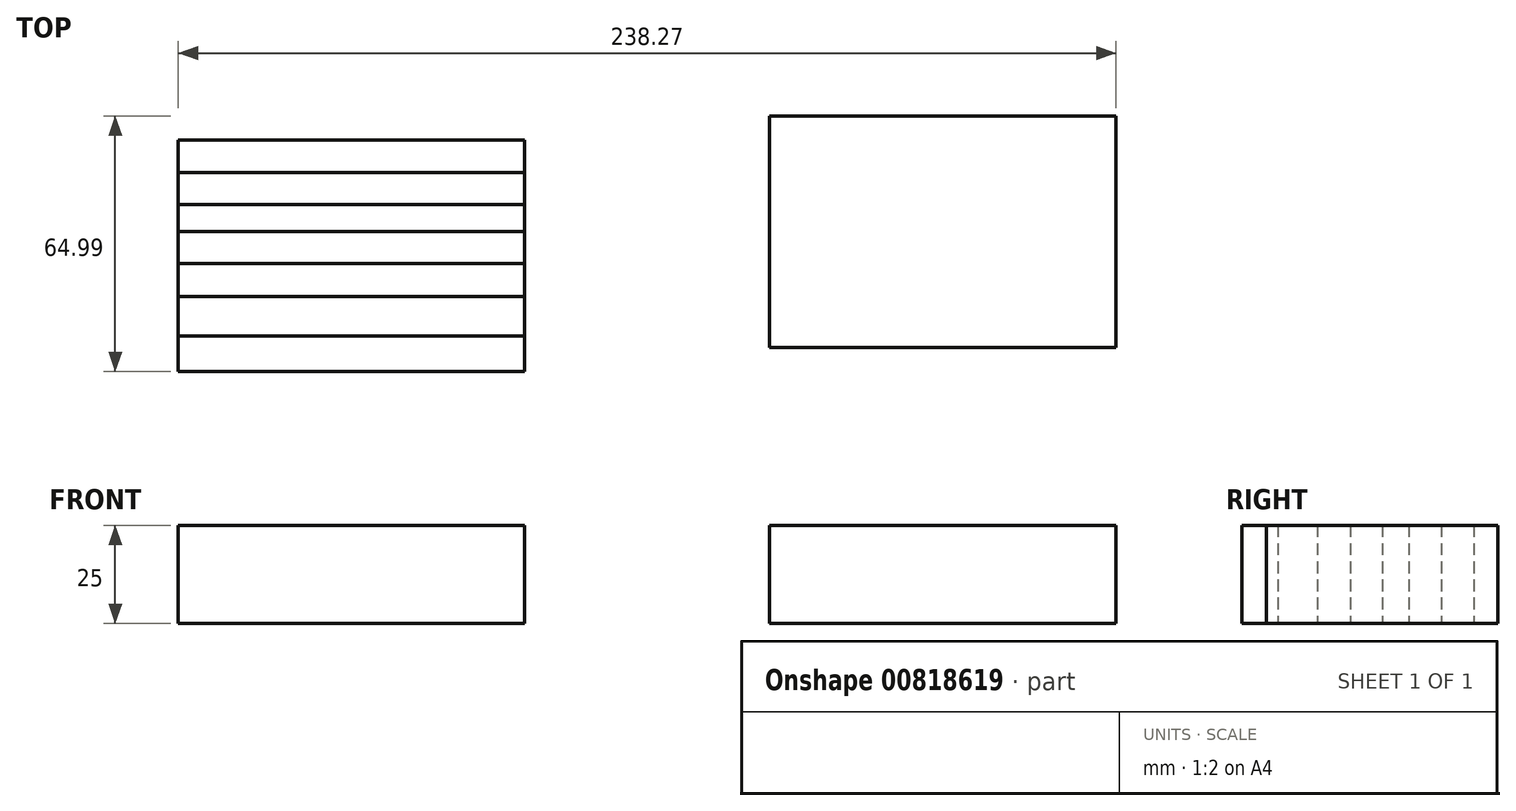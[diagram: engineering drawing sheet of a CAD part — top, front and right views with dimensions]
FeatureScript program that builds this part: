
annotation { "Feature Type Name" : "Feature", "Feature Type Description" : "" }
export const myFeature = defineFeature(function(context is Context, id is Id, definition is map)
    precondition{}
    {
        {
            var Q0;
            Q0=qCreatedBy(makeId("Top.planeOp"),FACE);
            var sketch = newSketch(context, id + "F0", { "sketchPlane" : qUnion([Q0])});
            skLineSegment(sketch, "E0.bottom", {"start": v(-107.96, 31.35) * mm, "end": v(-19.95, 31.35) * mm});
            skLineSegment(sketch, "E0.top", {"start": v(-107.96, -27.48) * mm, "end": v(-19.95, -27.48) * mm});
            skLineSegment(sketch, "E0.left", {"start": v(-107.96, 31.35) * mm, "end": v(-107.96, -27.48) * mm});
            skLineSegment(sketch, "E0.right", {"start": v(-19.95, 31.35) * mm, "end": v(-19.95, -27.48) * mm});
            skLineSegment(sketch, "E1.bottom", {"start": v(42.3, 37.5) * mm, "end": v(130.3, 37.5) * mm});
            skLineSegment(sketch, "E1.top", {"start": v(42.3, -21.32) * mm, "end": v(130.3, -21.32) * mm});
            skLineSegment(sketch, "E1.left", {"start": v(42.3, 37.5) * mm, "end": v(42.3, -21.32) * mm});
            skLineSegment(sketch, "E1.right", {"start": v(130.3, 37.5) * mm, "end": v(130.3, -21.32) * mm});
            skLineSegment(sketch, "E2", {"start": v(-107.96, 23.14) * mm, "end": v(-19.95, 23.14) * mm});
            skLineSegment(sketch, "E3", {"start": v(-107.96, 14.93) * mm, "end": v(-19.95, 14.93) * mm});
            skLineSegment(sketch, "E4", {"start": v(-107.96, 8.1) * mm, "end": v(-19.95, 8.1) * mm});
            skPoint(sketch, "E4.endSnap0", {"position": v(-19.95, 1.94) * mm});
            skLineSegment(sketch, "E5", {"start": v(-107.96, 0) * mm, "end": v(-19.95, 0) * mm});
            skLineSegment(sketch, "E6", {"start": v(-107.96, -8.32) * mm, "end": v(-19.95, -8.32) * mm});
            skLineSegment(sketch, "E7", {"start": v(-107.96, -18.36) * mm, "end": v(-19.95, -18.36) * mm});
            skSolve(sketch);
        }
        {
            var Q0;
            Q0=makeQuery(id+"F0.imprint","IMPRINT",FACE,{"disambiguationData":[TD([[makeQuery(id+"F0.imprint","IMPRINT",EDGE,{"derivedFrom":sQuery(id+"F0.wireOp",EDGE,"E1.bottom")}),-1.0]])]});
            extrude(context, id + "F1", {"entities" : qUnion([Q0]), "depth" : 25 * mm, "offsetDistance" : 25 * mm});
        }
        {
            var Q0;
            {var subQ0=sQuery(id+"F0.wireOp",EDGE,"E0.bottom");Q0=makeQuery(id+"F0.imprint","IMPRINT",FACE,{"disambiguationData":[TD([[makeQuery(id+"F0.imprint","IMPRINT",EDGE,{"derivedFrom":subQ0}),-1.0]])]});}
            extrude(context, id + "F2", {"entities" : qUnion([Q0]), "depth" : 25 * mm, "offsetDistance" : 25 * mm});
        }
        {
            var Q0;
            {var subQ0=sQuery(id+"F0.wireOp",EDGE,"E2");Q0=makeQuery(id+"F0.imprint","IMPRINT",FACE,{"disambiguationData":[TD([[makeQuery(id+"F0.imprint","IMPRINT",EDGE,{"derivedFrom":subQ0}),-1.0]])]});}
            extrude(context, id + "F3", {"entities" : qUnion([Q0]), "depth" : 25 * mm, "offsetDistance" : 25 * mm});
        }
        {
            var Q0;
            {var subQ0=sQuery(id+"F0.wireOp",EDGE,"E3");Q0=makeQuery(id+"F0.imprint","IMPRINT",FACE,{"disambiguationData":[TD([[makeQuery(id+"F0.imprint","IMPRINT",EDGE,{"derivedFrom":subQ0}),-1.0]])]});}
            extrude(context, id + "F4", {"entities" : qUnion([Q0]), "depth" : 25 * mm, "offsetDistance" : 25 * mm});
        }
        {
            var Q0;
            {var subQ0=sQuery(id+"F0.wireOp",EDGE,"E4");Q0=makeQuery(id+"F0.imprint","IMPRINT",FACE,{"disambiguationData":[TD([[makeQuery(id+"F0.imprint","IMPRINT",EDGE,{"derivedFrom":subQ0}),-1.0]])]});}
            extrude(context, id + "F5", {"entities" : qUnion([Q0]), "depth" : 25 * mm, "offsetDistance" : 25 * mm});
        }
        {
            var Q0;
            {var subQ0=sQuery(id+"F0.wireOp",EDGE,"E5");Q0=makeQuery(id+"F0.imprint","IMPRINT",FACE,{"disambiguationData":[TD([[makeQuery(id+"F0.imprint","IMPRINT",EDGE,{"derivedFrom":subQ0}),-1.0]])]});}
            extrude(context, id + "F6", {"entities" : qUnion([Q0]), "depth" : 25 * mm, "offsetDistance" : 25 * mm});
        }
        {
            var Q0;
            {var subQ0=sQuery(id+"F0.wireOp",EDGE,"E6");Q0=makeQuery(id+"F0.imprint","IMPRINT",FACE,{"disambiguationData":[TD([[makeQuery(id+"F0.imprint","IMPRINT",EDGE,{"derivedFrom":subQ0}),-1.0]])]});}
            extrude(context, id + "F7", {"entities" : qUnion([Q0]), "depth" : 25 * mm, "offsetDistance" : 25 * mm});
        }
        {
            var Q0;
            {var subQ0=sQuery(id+"F0.wireOp",EDGE,"E0.top");Q0=makeQuery(id+"F0.imprint","IMPRINT",FACE,{"disambiguationData":[TD([[makeQuery(id+"F0.imprint","IMPRINT",EDGE,{"derivedFrom":subQ0}),1.0]])]});}
            extrude(context, id + "F8", {"entities" : qUnion([Q0]), "depth" : 25 * mm, "offsetDistance" : 25 * mm});
        }
    });
